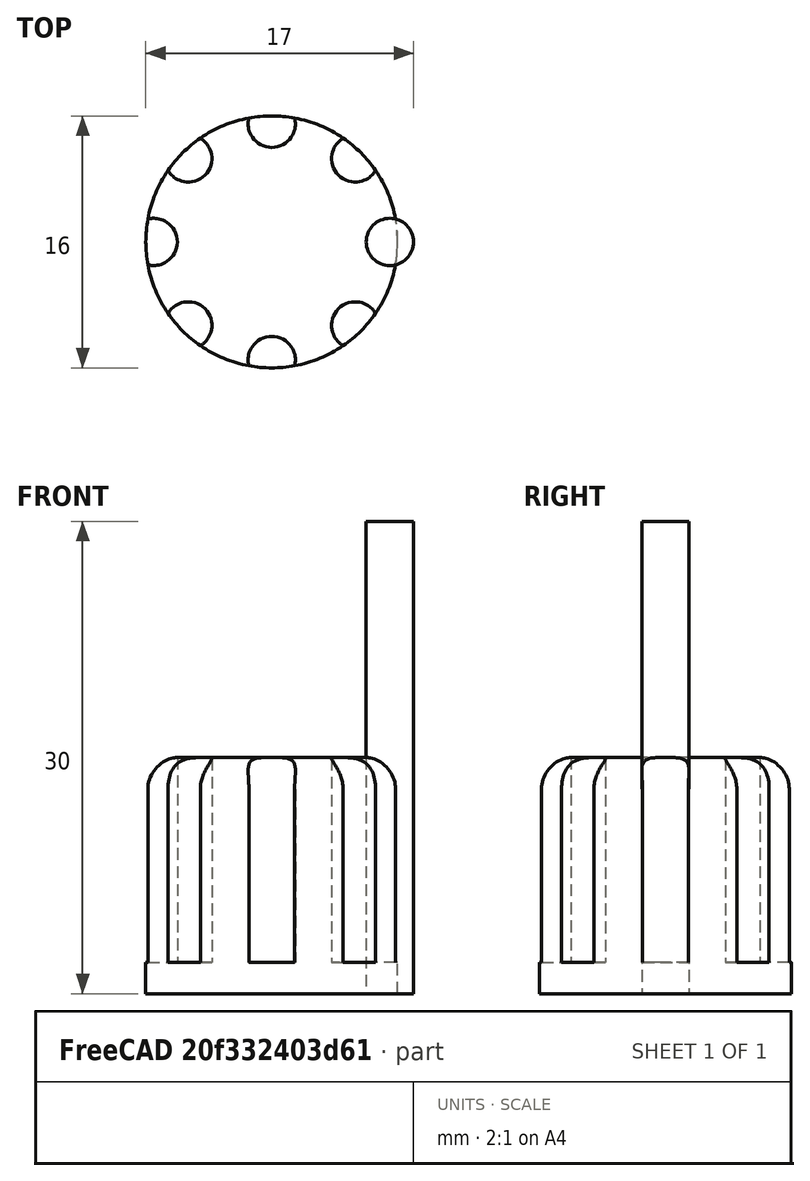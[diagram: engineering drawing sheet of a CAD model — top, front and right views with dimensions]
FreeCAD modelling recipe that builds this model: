
FCSTD DOCUMENT  (FreeCAD 1.0R39319 (Git))
Label: ojt1_t12r01_buttom_potenciometer
License: All rights reserved
LicenseURL: https://en.wikipedia.org/wiki/All_rights_reserved
objects: Part::Cylinder×2, Part::FeaturePython×1, Part::Fillet×1, Part::Cut×1
note: 4 computed .brp shape members not serialized (recipe doc carries the construction recipe); baked Part::Feature solids carry a one-line shape summary decoded from their .brp

FEATURE [Part::Cylinder] Cylinder  label="Cilindre"
  Angle = 360
  AttacherType = Attacher::AttachEngine3D
  FirstAngle = 0
  Height = 15
  Radius = 8
  SecondAngle = 0
FEATURE [Part::Cylinder] Cylinder001  label="Cilindre001"
  Angle = 360
  AttacherType = Attacher::AttachEngine3D
  FirstAngle = 0
  Height = 30
  Placement = pos=(7.5,0,0) rot=(0,0,1;0rad)
  Radius = 1.5
  SecondAngle = 0
FEATURE [Part::FeaturePython] Array  # Draft array (typed FeaturePython)
  AlwaysSyncPlacement = false
  Angle = 360
  ArrayType = 1
  Axis = (0,0,1)
  Base = -> Cylinder001
  Center = (0,0,0)
  Count = 8
  ExpandArray = false
  Fuse = false
  IntervalAxis = (0,0,0)
  IntervalX = (50,0,0)
  IntervalY = (0,50,0)
  IntervalZ = (0,0,50)
  NumberCircles = 3
  NumberPolar = 8
  NumberX = 2
  NumberY = 2
  NumberZ = 1
  Placement = pos=(0,0,2) rot=(0,0,1;0rad)
  PlacementList = 8 placements: [(7.5,0,0),(5.3033,5.3033,0),(0,7.5,0),(-5.3033,5.3033,0),(-7.5,9.18485e-16,0),(-5.3033,-5.3033,0),(-1.66533e-15,-7.5,0),(5.3033,-5.3033,0)]
  RadialDistance = 50
  ScaleList = (8) [(1,1,1),(1,1,1),(1,1,1),(1,1,1),(1,1,1),(1,1,1),(1,1,1),(1,1,1)]
  Symmetry = 1
  TangentialDistance = 25
FEATURE [Part::Fillet] Fillet
  Base = -> Cylinder
  EdgeLinks = -> Cylinder [Edge3]
  Edges = 1 edges r=2: [Edge3]
FEATURE [Part::Cut] Cut
  Base = -> Fillet
  Refine = true
  Tool = -> Array
